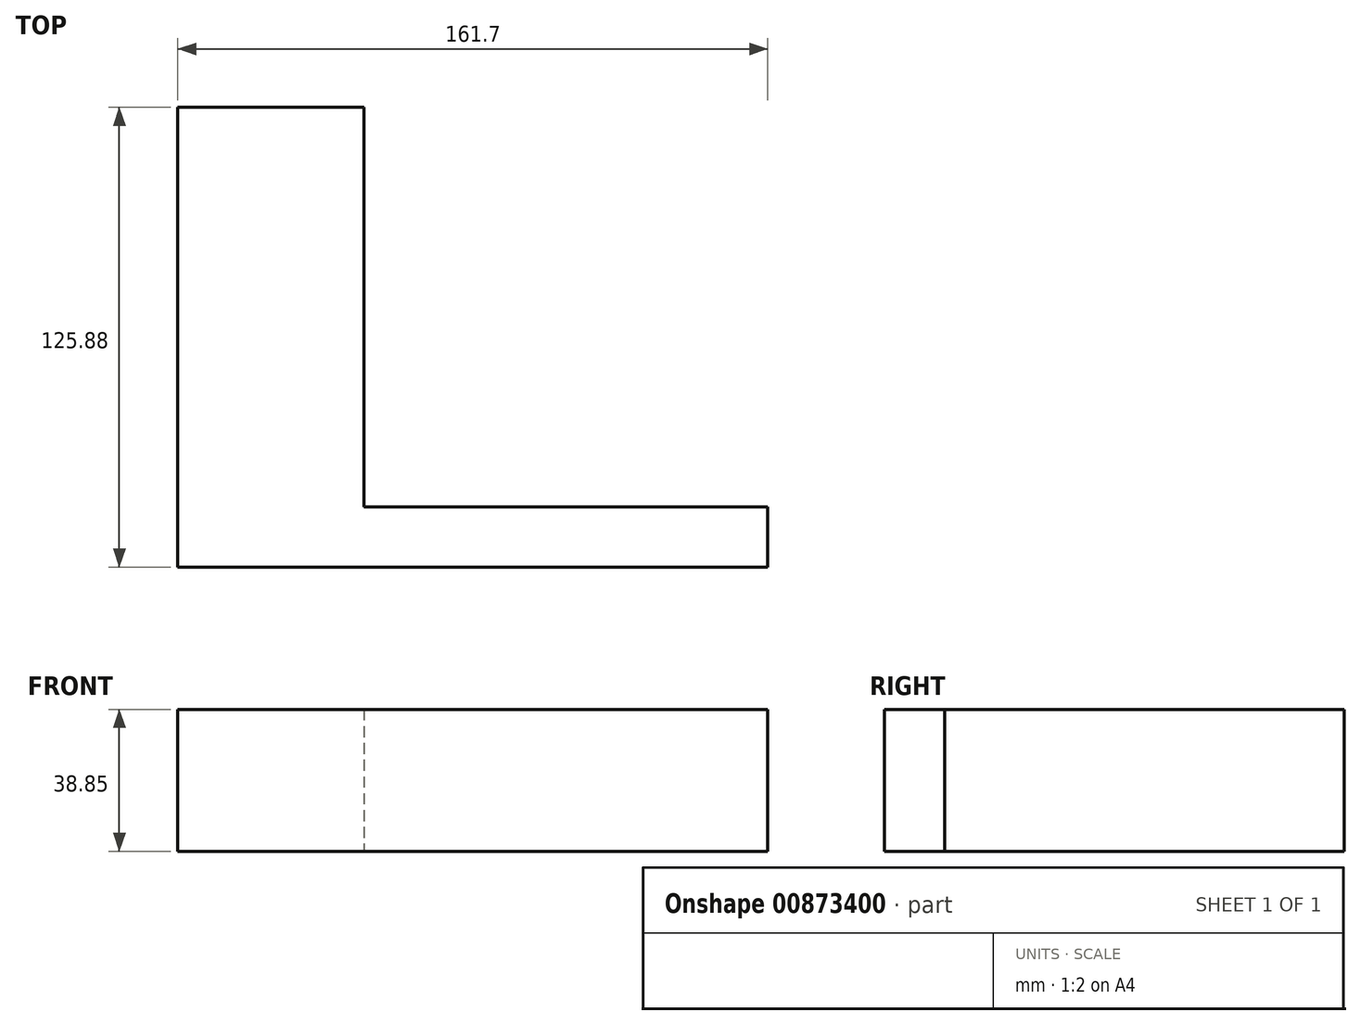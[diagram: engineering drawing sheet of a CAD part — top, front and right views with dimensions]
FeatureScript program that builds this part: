
annotation { "Feature Type Name" : "Feature", "Feature Type Description" : "" }
export const myFeature = defineFeature(function(context is Context, id is Id, definition is map)
    precondition{}
    {
        {
            var Q0;
            Q0=qCreatedBy(makeId("Top.planeOp"),FACE);
            var sketch = newSketch(context, id + "F0", { "sketchPlane" : qUnion([Q0])});
            skLineSegment(sketch, "E0.bottom", {"start": v(74.76, 75.1) * mm, "end": v(-35.98, 75.1) * mm});
            skLineSegment(sketch, "E0.top", {"start": v(74.76, 58.61) * mm, "end": v(-35.98, 58.61) * mm});
            skLineSegment(sketch, "E0.left", {"start": v(74.76, 75.1) * mm, "end": v(74.76, 58.61) * mm});
            skLineSegment(sketch, "E0.right", {"start": v(-35.98, 75.1) * mm, "end": v(-35.98, 58.61) * mm});
            skLineSegment(sketch, "E1.bottom", {"start": v(-35.98, 58.61) * mm, "end": v(-86.94, 58.61) * mm});
            skLineSegment(sketch, "E1.top", {"start": v(-35.98, 184.5) * mm, "end": v(-86.94, 184.5) * mm});
            skLineSegment(sketch, "E1.left", {"start": v(-35.98, 58.61) * mm, "end": v(-35.98, 184.5) * mm});
            skLineSegment(sketch, "E1.right", {"start": v(-86.94, 58.61) * mm, "end": v(-86.94, 184.5) * mm});
            skSolve(sketch);
        }
        {
            var Q0;
            Q0 = qSketchRegion(id + "F0", true);
            extrude(context, id + "F1", {"entities" : qUnion([Q0]), "depth" : 38.85 * mm, "offsetDistance" : 25.4 * mm});
        }
    });
